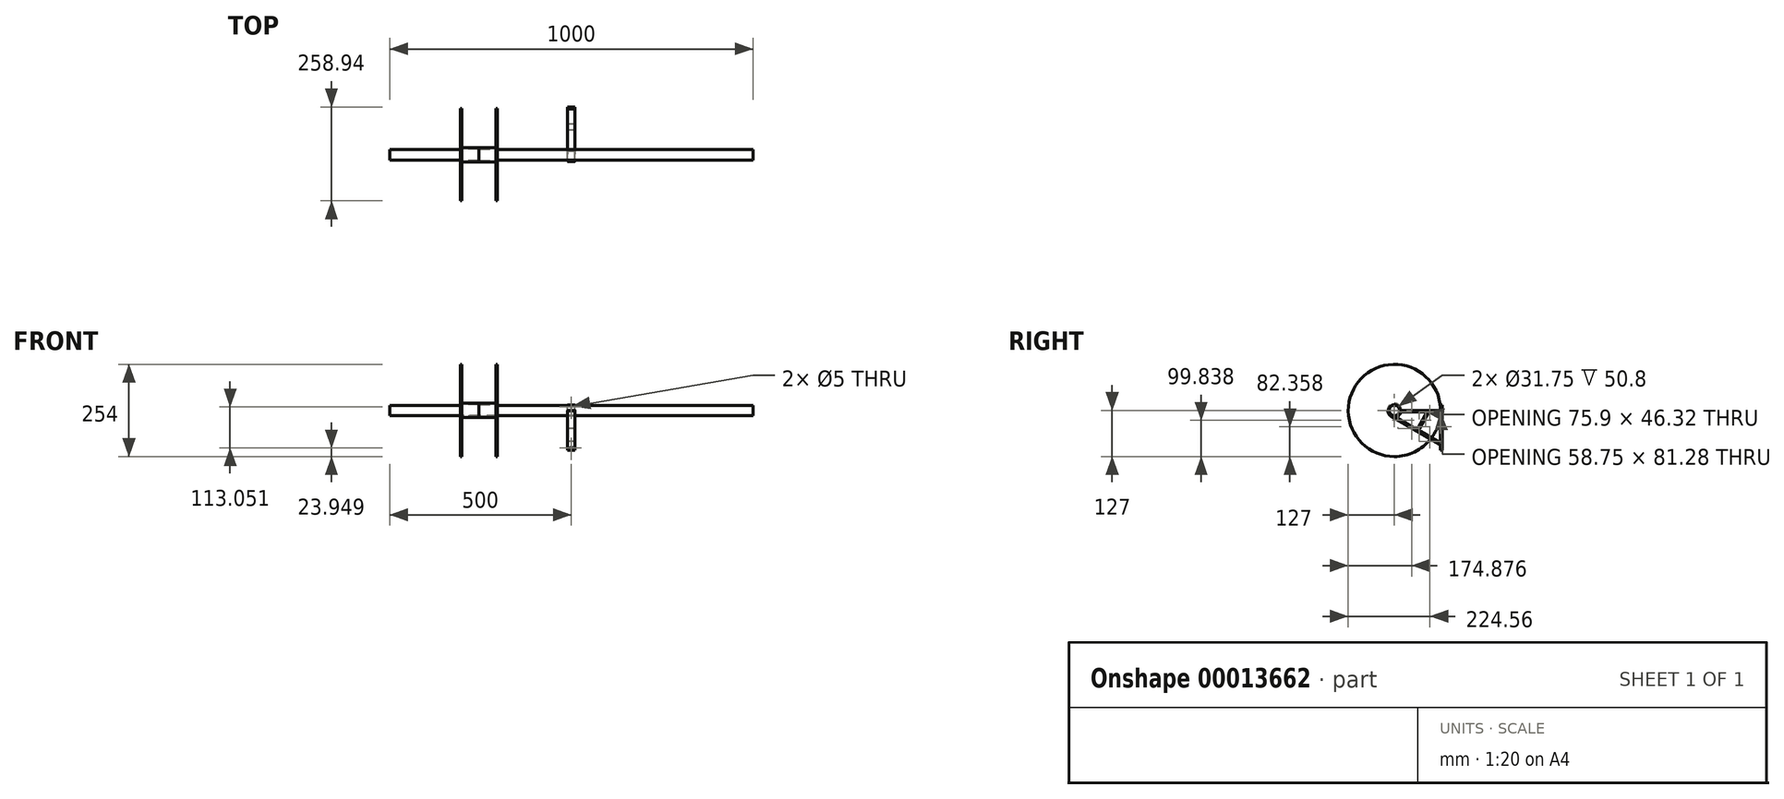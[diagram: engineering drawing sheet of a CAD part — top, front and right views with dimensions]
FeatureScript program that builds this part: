
annotation { "Feature Type Name" : "Feature", "Feature Type Description" : "" }
export const myFeature = defineFeature(function(context is Context, id is Id, definition is map)
    precondition{}
    {
        {
            var Q0;
            Q0=qCreatedBy(makeId("Right.planeOp"),FACE);
            var sketch = newSketch(context, id + "F0", { "sketchPlane" : qUnion([Q0])});
            skCircle(sketch, "E0", {"center": v(0, 0) * mm, "radius": 14.29 * mm});
            skSolve(sketch);
        }
        {
            var Q0;
            Q0 = qSketchRegion(id + "F0", true);
            extrude(context, id + "F1", {"entities" : qUnion([Q0]), "endBound" : BoundingType.SYMMETRIC, "depth" : 1000 * mm});
        }
        {
            var Q0;
            Q0=qCreatedBy(makeId("Front.planeOp"),FACE);
            var sketch = newSketch(context, id + "F2", { "sketchPlane" : qUnion([Q0])});
            skLineSegment(sketch, "E1", {"start": v(0, 0) * mm, "end": v(-488.1, 0) * mm, "construction": true});
            skLineSegment(sketch, "E2", {"start": v(-254, 15.87) * mm, "end": v(-203.2, 15.88) * mm});
            skLineSegment(sketch, "E3", {"start": v(-203.2, 15.88) * mm, "end": v(-203.2, 127) * mm});
            skLineSegment(sketch, "E4", {"start": v(-203.2, 127) * mm, "end": v(-207.01, 127) * mm});
            skLineSegment(sketch, "E5", {"start": v(-207.01, 127) * mm, "end": v(-207.01, 19.69) * mm});
            skLineSegment(sketch, "E6", {"start": v(-207.01, 19.69) * mm, "end": v(-254, 19.69) * mm});
            skLineSegment(sketch, "E7", {"start": v(-254, 19.69) * mm, "end": v(-254, 15.87) * mm});
            skLineSegment(sketch, "E8", {"start": v(-254, 15.87) * mm, "end": v(-254, -25.3) * mm, "construction": true});
            skSolve(sketch);
        }
        {
            var Q0;
            Q0 = qSketchRegion(id + "F2", true);
            var Q1;
            Q1=sQuery(id+"F2.wireOp",EDGE,"E1");
            revolve(context, id + "F3", {"entities" : qUnion([Q0]), "axis" : qUnion([Q1]), "revolveType" : RevolveType.FULL});
        }
        {
            var Q0;
            Q0=makeQuery(id+"F3.opRevolve","SWEPT_BODY",BODY,{"disambiguationData":[OSD([sQuery(id+"F2.wireOp",EDGE,"E2"),sQuery(id+"F2.wireOp",EDGE,"E3"),sQuery(id+"F2.wireOp",EDGE,"E4"),sQuery(id+"F2.wireOp",EDGE,"E5"),sQuery(id+"F2.wireOp",EDGE,"E6"),sQuery(id+"F2.wireOp",EDGE,"E7")])]});
            var Q1;
            Q1=makeQuery(id+"F3.opRevolve","SWEPT_FACE",FACE,{"disambiguationData":[OSD([sQuery(id+"F2.wireOp",EDGE,"E7")])]});
            mirror(context, id + "F4", {"operationType" : NewBodyOperationType.ADD, "entities" : qUnion([Q0]), "mirrorPlane" : qUnion([Q1])});
        }
        {
            var Q0;
            Q0=qCreatedBy(makeId("Right.planeOp"),FACE);
            var sketch = newSketch(context, id + "F5", { "sketchPlane" : qUnion([Q0])});
            skArc(sketch, "E9", {"start": v(-15.24, 0) * mm, "mid": v(0, -15.24) * mm, "end": v(15.24, 0) * mm});
            skArc(sketch, "E10", {"start": v(-18.41, 0) * mm, "mid": v(-15.95, -9.2) * mm, "end": v(-9.2, -15.95) * mm});
            skLineSegment(sketch, "E11", {"start": v(-15.24, 0) * mm, "end": v(-18.41, 0) * mm});
            skLineSegment(sketch, "E12", {"start": v(15.24, 0) * mm, "end": v(18.41, 0) * mm});
            skArc(sketch, "E13", {"start": v(126.94, 4) * mm, "mid": v(-127, 0) * mm, "end": v(126.94, -4) * mm, "construction": true});
            skLineSegment(sketch, "E14", {"start": v(18.41, 0) * mm, "end": v(126.94, 0) * mm});
            skLineSegment(sketch, "E15", {"start": v(131.94, -109.55) * mm, "end": v(126.94, -109.55) * mm});
            skLineSegment(sketch, "E16", {"start": v(126.94, -109.55) * mm, "end": v(126.94, -94.55) * mm});
            skLineSegment(sketch, "E17", {"start": v(126.94, -4) * mm, "end": v(95.1, -4) * mm});
            skLineSegment(sketch, "E18", {"start": v(126.94, -89.93) * mm, "end": v(65.85, -54.66) * mm});
            skLineSegment(sketch, "E19", {"start": v(126.94, -94.55) * mm, "end": v(-9.2, -15.95) * mm});
            skLineSegment(sketch, "E20.top", {"start": v(131.94, 15) * mm, "end": v(126.94, 15) * mm});
            skLineSegment(sketch, "E20.right", {"start": v(126.94, 0) * mm, "end": v(126.94, 15) * mm});
            skLineSegment(sketch, "E21", {"start": v(131.94, 15) * mm, "end": v(131.94, -109.55) * mm});
            skArc(sketch, "E22.trimOffspring", {"start": v(2.72, -18.21) * mm, "mid": v(12.55, -13.47) * mm, "end": v(17.98, -4) * mm});
            skLineSegment(sketch, "E23.trimOffspring", {"start": v(126.94, -89.93) * mm, "end": v(126.94, -4) * mm});
            skLineSegment(sketch, "E24", {"start": v(95.1, -4) * mm, "end": v(65.85, -54.66) * mm});
            skLineSegment(sketch, "E25", {"start": v(62.38, -52.66) * mm, "end": v(90.48, -4) * mm});
            skLineSegment(sketch, "E26.trimOffspring", {"start": v(90.48, -4) * mm, "end": v(17.98, -4) * mm});
            skLineSegment(sketch, "E27.trimOffspring", {"start": v(62.38, -52.66) * mm, "end": v(2.72, -18.21) * mm});
            skSolve(sketch);
        }
        {
            var Q0;
            Q0 = qSketchRegion(id + "F5", true);
            extrude(context, id + "F6", {"entities" : qUnion([Q0]), "endBound" : BoundingType.SYMMETRIC, "depth" : 20 * mm});
        }
        {
            var Q0;
            Q0=makeQuery(id+"F6.opExtrude","SWEPT_EDGE",EDGE,{"disambiguationData":[OSD([sQuery(id+"F5.wireOp",EDGE,"E16"),sQuery(id+"F5.wireOp",EDGE,"E19")])]});
            var Q1;
            Q1=makeQuery(id+"F6.opExtrude","SWEPT_EDGE",EDGE,{"disambiguationData":[OSD([sQuery(id+"F5.wireOp",EDGE,"E17"),sQuery(id+"F5.wireOp",EDGE,"E23.trimOffspring")])]});
            var Q2;
            Q2=makeQuery(id+"F6.opExtrude","SWEPT_EDGE",EDGE,{"disambiguationData":[OSD([sQuery(id+"F5.wireOp",EDGE,"E17"),sQuery(id+"F5.wireOp",EDGE,"E22.trimOffspring")])]});
            var Q3;
            Q3=makeQuery(id+"F6.opExtrude","SWEPT_EDGE",EDGE,{"disambiguationData":[OSD([sQuery(id+"F5.wireOp",EDGE,"E16"),sQuery(id+"F5.wireOp",EDGE,"E19")])]});
            var Q4;
            Q4=makeQuery(id+"F6.opExtrude","SWEPT_EDGE",EDGE,{"disambiguationData":[OSD([sQuery(id+"F5.wireOp",EDGE,"E18"),sQuery(id+"F5.wireOp",EDGE,"E23.trimOffspring")])]});
            var Q5;
            Q5=makeQuery(id+"F6.opExtrude","SWEPT_EDGE",EDGE,{"disambiguationData":[OSD([sQuery(id+"F5.wireOp",EDGE,"E18"),sQuery(id+"F5.wireOp",EDGE,"E22.trimOffspring")])]});
            var Q6;
            Q6=makeQuery(id+"F6.opExtrude","SWEPT_EDGE",EDGE,{"disambiguationData":[OSD([sQuery(id+"F5.wireOp",EDGE,"E10"),sQuery(id+"F5.wireOp",EDGE,"E19")])]});
            var Q7;
            Q7=makeQuery(id+"F6.opExtrude","SWEPT_EDGE",EDGE,{"disambiguationData":[OSD([sQuery(id+"F5.wireOp",EDGE,"E18"),sQuery(id+"F5.wireOp",EDGE,"E23.trimOffspring")])]});
            var Q8;
            Q8=makeQuery(id+"F6.opExtrude","SWEPT_EDGE",EDGE,{"disambiguationData":[OSD([sQuery(id+"F5.wireOp",EDGE,"E18"),sQuery(id+"F5.wireOp",EDGE,"E22.trimOffspring")])]});
            var Q9;
            Q9=makeQuery(id+"F6.opExtrude","SWEPT_EDGE",EDGE,{"disambiguationData":[OSD([sQuery(id+"F5.wireOp",EDGE,"E10"),sQuery(id+"F5.wireOp",EDGE,"E19")])]});
            var Q10;
            Q10=makeQuery(id+"F6.opExtrude","SWEPT_EDGE",EDGE,{"disambiguationData":[OSD([sQuery(id+"F5.wireOp",EDGE,"E17"),sQuery(id+"F5.wireOp",EDGE,"E23.trimOffspring")])]});
            var Q11;
            Q11=makeQuery(id+"F6.opExtrude","SWEPT_EDGE",EDGE,{"disambiguationData":[OSD([sQuery(id+"F5.wireOp",EDGE,"E17"),sQuery(id+"F5.wireOp",EDGE,"E22.trimOffspring")])]});
            var Q12;
            Q12=makeQuery(id+"F6.opExtrude","SWEPT_EDGE",EDGE,{"disambiguationData":[OSD([sQuery(id+"F5.wireOp",EDGE,"E16"),sQuery(id+"F5.wireOp",EDGE,"E19")])]});
            var Q13;
            Q13=makeQuery(id+"F6.opExtrude","SWEPT_EDGE",EDGE,{"disambiguationData":[OSD([sQuery(id+"F5.wireOp",EDGE,"E17"),sQuery(id+"F5.wireOp",EDGE,"E23.trimOffspring")])]});
            var Q14;
            Q14=makeQuery(id+"F6.opExtrude","SWEPT_EDGE",EDGE,{"disambiguationData":[OSD([sQuery(id+"F5.wireOp",EDGE,"E17"),sQuery(id+"F5.wireOp",EDGE,"E22.trimOffspring")])]});
            var Q15;
            Q15=makeQuery(id+"F6.opExtrude","SWEPT_EDGE",EDGE,{"disambiguationData":[OSD([sQuery(id+"F5.wireOp",EDGE,"E14"),sQuery(id+"F5.wireOp",EDGE,"E20.right")])]});
            var Q16;
            Q16=makeQuery(id+"F6.opExtrude","SWEPT_EDGE",EDGE,{"disambiguationData":[OSD([sQuery(id+"F5.wireOp",EDGE,"E16"),sQuery(id+"F5.wireOp",EDGE,"E19")])]});
            var Q17;
            Q17=makeQuery(id+"F6.opExtrude","SWEPT_EDGE",EDGE,{"disambiguationData":[OSD([sQuery(id+"F5.wireOp",EDGE,"E9"),sQuery(id+"F5.wireOp",EDGE,"E12")])]});
            var Q18;
            Q18=makeQuery(id+"F6.opExtrude","SWEPT_EDGE",EDGE,{"disambiguationData":[OSD([sQuery(id+"F5.wireOp",EDGE,"E25"),sQuery(id+"F5.wireOp",EDGE,"E26.trimOffspring")])]});
            var Q19;
            Q19=makeQuery(id+"F6.opExtrude","SWEPT_EDGE",EDGE,{"disambiguationData":[OSD([sQuery(id+"F5.wireOp",EDGE,"E25"),sQuery(id+"F5.wireOp",EDGE,"E27.trimOffspring")])]});
            fillet(context, id + "F7", {"entities" : qUnion([Q0, Q1, Q2, Q3, Q4, Q5, Q6, Q7, Q8, Q9, Q10, Q11, Q12, Q13, Q14, Q15, Q16, Q17, Q18, Q19]), "radius" : 6.35 * mm, "tangentPropagation" : true, "allowEdgeOverflow" : false});
        }
        {
            var Q0;
            {var subQ0=sQuery(id+"F5.wireOp",EDGE,"E16");Q0=makeQuery(id+"F6.opExtrude","SWEPT_FACE",FACE,{"disambiguationData":[OSD([subQ0]),TDD([makeQuery(id+"F5.imprint","IMPRINT",EDGE,{"disambiguationData":[TD([[makeQuery(id+"F5.imprint","INTERSECT",VERTEX,{"derivedFrom":[sQuery(id+"F5.wireOp",EDGE,"E15"),subQ0]}),-1.0]])],"derivedFrom":subQ0})])]});}
            var sketch = newSketch(context, id + "F8", { "sketchPlane" : qUnion([Q0])});
            skPoint(sketch, "E28", {"position": v(0, 10) * mm});
            skPoint(sketch, "E29", {"position": v(0, -103.05) * mm});
            skLineSegment(sketch, "E30", {"start": v(-10, -103.05) * mm, "end": v(10, -103.05) * mm, "construction": true});
            skSolve(sketch);
        }
        {
            var Q0;
            Q0=sQuery(id+"F8.wireOp",VERTEX,"E28");
            var Q1;
            Q1=sQuery(id+"F8.wireOp",VERTEX,"E29");
            var Q2;
            Q2=makeQuery(id+"F6.opExtrude","SWEPT_BODY",BODY,{"disambiguationData":[OSD([sQuery(id+"F5.wireOp",EDGE,"E9"),sQuery(id+"F5.wireOp",EDGE,"E10"),sQuery(id+"F5.wireOp",EDGE,"E11"),sQuery(id+"F5.wireOp",EDGE,"E12"),sQuery(id+"F5.wireOp",EDGE,"E14"),sQuery(id+"F5.wireOp",EDGE,"7c791220-ecef-45b2-95ab-84f3ec04a31d"),sQuery(id+"F5.wireOp",EDGE,"E15"),sQuery(id+"F5.wireOp",EDGE,"E16"),sQuery(id+"F5.wireOp",EDGE,"E17"),sQuery(id+"F5.wireOp",EDGE,"E18"),sQuery(id+"F5.wireOp",EDGE,"E19"),sQuery(id+"F5.wireOp",EDGE,"E20.top"),sQuery(id+"F5.wireOp",EDGE,"E20.left"),sQuery(id+"F5.wireOp",EDGE,"E20.right")])]});
            hole(context, id + "F9", {"style" : HoleStyle.SIMPLE, "holeDiameter" : 5 * mm, "endStyle" : HoleEndStyle.THROUGH, "locations" : qUnion([Q0, Q1]), "scope" : qUnion([Q2]), "isTappedThrough" : true});
        }
        {
            var Q0;
            Q0=makeQuery(id+"F6.opExtrude","SWEPT_EDGE",EDGE,{"disambiguationData":[OSD([sQuery(id+"F5.wireOp",EDGE,"E9"),sQuery(id+"F5.wireOp",EDGE,"E11")])]});
            var Q1;
            Q1=makeQuery(id+"F6.opExtrude","SWEPT_EDGE",EDGE,{"disambiguationData":[OSD([sQuery(id+"F5.wireOp",EDGE,"E10"),sQuery(id+"F5.wireOp",EDGE,"E11")])]});
            fillet(context, id + "F10", {"entities" : qUnion([Q0, Q1]), "radius" : 1 * mm, "tangentPropagation" : true, "allowEdgeOverflow" : false});
        }
    });
